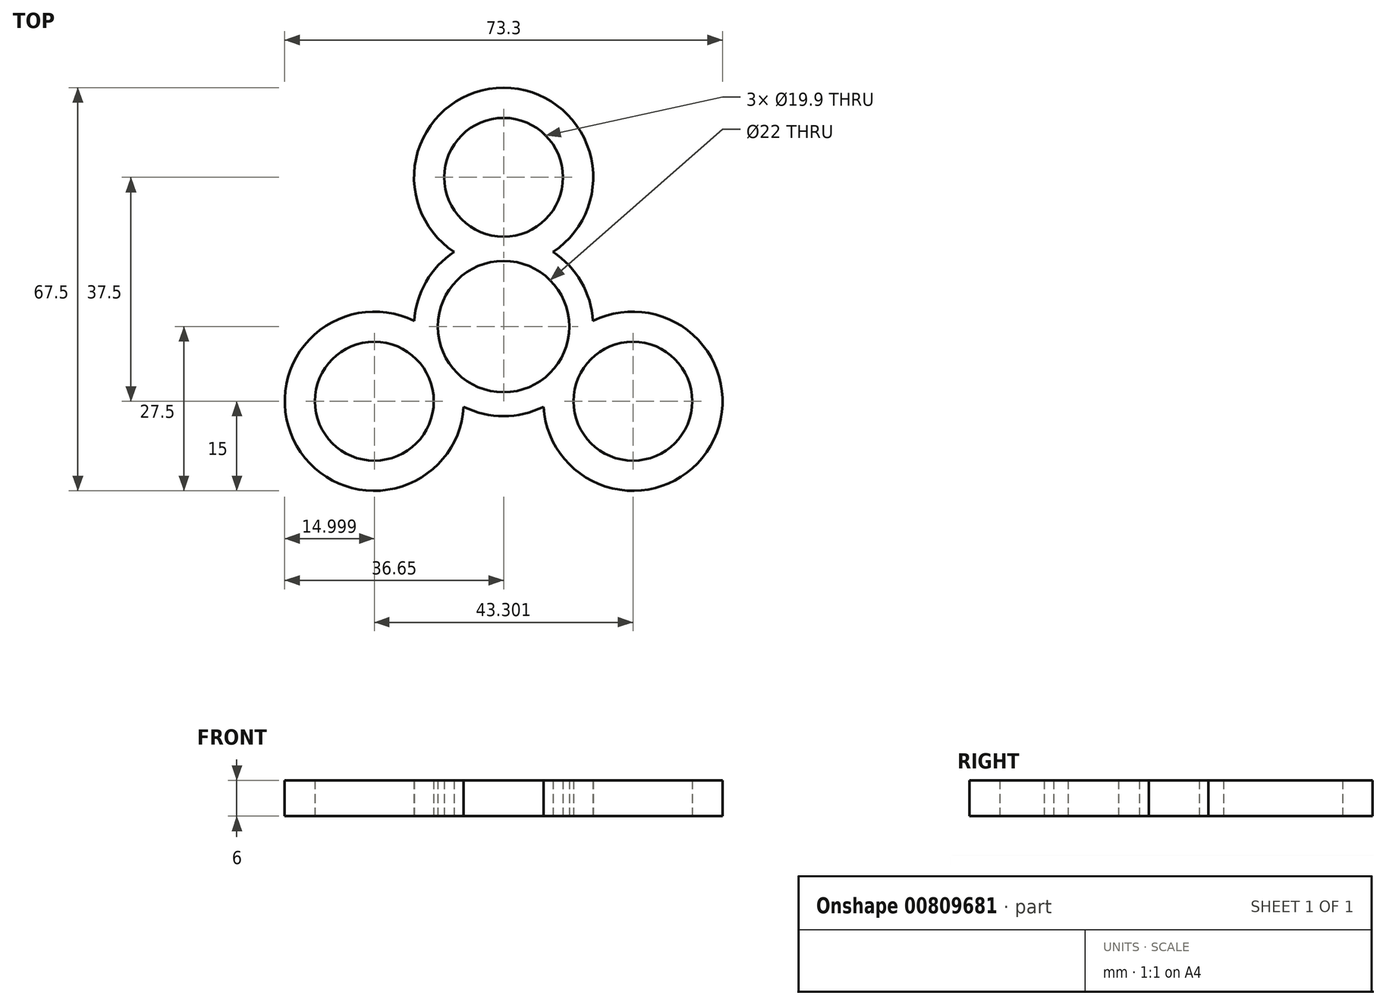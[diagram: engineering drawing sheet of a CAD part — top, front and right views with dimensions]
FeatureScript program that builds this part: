
annotation { "Feature Type Name" : "Feature", "Feature Type Description" : "" }
export const myFeature = defineFeature(function(context is Context, id is Id, definition is map)
    precondition{}
    {
        {
            var Q0;
            Q0=qCreatedBy(makeId("Top.planeOp"),FACE);
            var sketch = newSketch(context, id + "F0", { "sketchPlane" : qUnion([Q0])});
            skArc(sketch, "E0", {"start": v(9.53, 5.5) * mm, "mid": v(0, 11) * mm, "end": v(-9.53, 5.5) * mm});
            skLineSegment(sketch, "E1", {"start": v(0, 0) * mm, "end": v(0, 25) * mm});
            skArc(sketch, "E2", {"start": v(-8.3, 12.5) * mm, "mid": v(-10.93, 10.27) * mm, "end": v(-13, 7.5) * mm});
            skCircle(sketch, "E3", {"center": v(0, 25) * mm, "radius": 9.95 * mm});
            skArc(sketch, "E4.trimOffspring", {"start": v(13, 7.5) * mm, "mid": v(10.93, 10.27) * mm, "end": v(8.3, 12.5) * mm});
            skArc(sketch, "E5.trimOffspring", {"start": v(8.3, 12.5) * mm, "mid": v(0, 40) * mm, "end": v(-8.3, 12.5) * mm});
            skArc(sketch, "E6.1.0", {"start": v(-14.97, 0.93) * mm, "mid": v(-34.64, -20) * mm, "end": v(-6.68, -13.43) * mm});
            skCircle(sketch, "E6.1.1", {"center": v(-21.65, -12.5) * mm, "radius": 9.95 * mm});
            skArc(sketch, "E6.1.2", {"start": v(-9.53, 5.5) * mm, "mid": v(-9.53, -5.5) * mm, "end": v(0, -11) * mm});
            skArc(sketch, "E6.1.3", {"start": v(-6.68, -13.43) * mm, "mid": v(-3.43, -14.6) * mm, "end": v(0, -15) * mm});
            skArc(sketch, "E6.1.4", {"start": v(-13, 7.5) * mm, "mid": v(-14.36, 4.33) * mm, "end": v(-14.97, 0.93) * mm});
            skArc(sketch, "E6.2.0", {"start": v(6.68, -13.43) * mm, "mid": v(34.64, -20) * mm, "end": v(14.97, 0.93) * mm});
            skCircle(sketch, "E6.2.1", {"center": v(21.65, -12.5) * mm, "radius": 9.95 * mm});
            skArc(sketch, "E6.2.2", {"start": v(0, -11) * mm, "mid": v(9.53, -5.5) * mm, "end": v(9.53, 5.5) * mm});
            skArc(sketch, "E6.2.3", {"start": v(14.97, 0.93) * mm, "mid": v(14.36, 4.33) * mm, "end": v(13, 7.5) * mm});
            skArc(sketch, "E6.2.4", {"start": v(0, -15) * mm, "mid": v(3.43, -14.6) * mm, "end": v(6.68, -13.43) * mm});
            skSolve(sketch);
        }
        {
            var Q0;
            Q0 = qSketchRegion(id + "F0", true);
            extrude(context, id + "F1", {"entities" : qUnion([Q0]), "depth" : 6 * mm, "offsetDistance" : 25 * mm});
        }
    });
